# Revit family: BE_99396_de_DE
name_source: partatom
category: Leuchten
revit_build: Autodesk Revit 2015 (Build: 20150704_0715(x64)
units: mm (PartAtom-declared; Revit-internal decimal feet)

## types (2) — shared parameters
AC/DC = DC
Aktualisierung = 2015-10-27T04:08:49
BEGA_Dummy = Nein
BEGA_IES = Ja
BEGA_Intern = Ja
BEGA_Intern_Konstruktion = Ja
BEGA_Intern_an = Ja
BEGA_Intern_aus = Ja
Befestigungsbohrung = Ø 70 mm
Beschreibung = Bodeneinbauleuchte
Beschreibung_Sonderanfertigung = Hier können Sie Informationen zur Sonderanfertigung eintragen.
Bestellnummer_Einbaugehäuse = ---
CE_Konformität = ja
Einbau_in_Wärmedämmung = ungeeignet
Einbaugehäuse = Nein
Einbautiefe = 100 mm
Einbauöffnung = 70 mm
Energieeffizienzklasse = LED A++ - A
Farbfilter = 16777215
Farbtemperaturverschiebung bei Dämpfen der Lampe = <Keine Auswahl>
Farbwiedergabeindex = Ra > 80
Gewicht = 0.8 kg
Hersteller = BEGA
Lampe = LED 4.5 W
Lastklassifizierung = Beleuchtung
Lebensdauerkriterien = L70 = 50.000 h
Leuchtenlichtstrom = 286 lm
Logo = BEGA_Logo.png
Material_09 = BEGA_Glas_klar
Material_15 = BEGA_Leuchtmedium_matt
Material_17 = BEGA_Reflektor
Material_18 = BEGA_Gummi_schwarz
Neigungswinkel = 0.00°
Oberflächentemperatur = 35 °C
Produktdatenblatt = http://www.bega.de
Scheinlast = 0 VA
Schutzart = IP 68...20 m
Schutzklasse = III
Sonderanfertigung = Nein
Spannung = 0 V
Typenbild = 99396.png
URL = http://www.bega.de
zero-valued in all types: Vorgabe-Ansicht

## per-type parameters (varying)
| type | Bestellnummer | Datei für fotometrisches Netz | Farbtemperatur | LED_Modulbezeichnung | Lampenlichtstrom | Modell |
| BEGA_99396_K4 | 99396 | BE_99396.IES | 4000 K | LED-0386/840 | 520 lm | 99396 |
| BEGA_99396_K3 | 99396K3 | BE_99396K3.IES | 3000 K | LED-0386/830 | 480 lm | 99396K3 |
